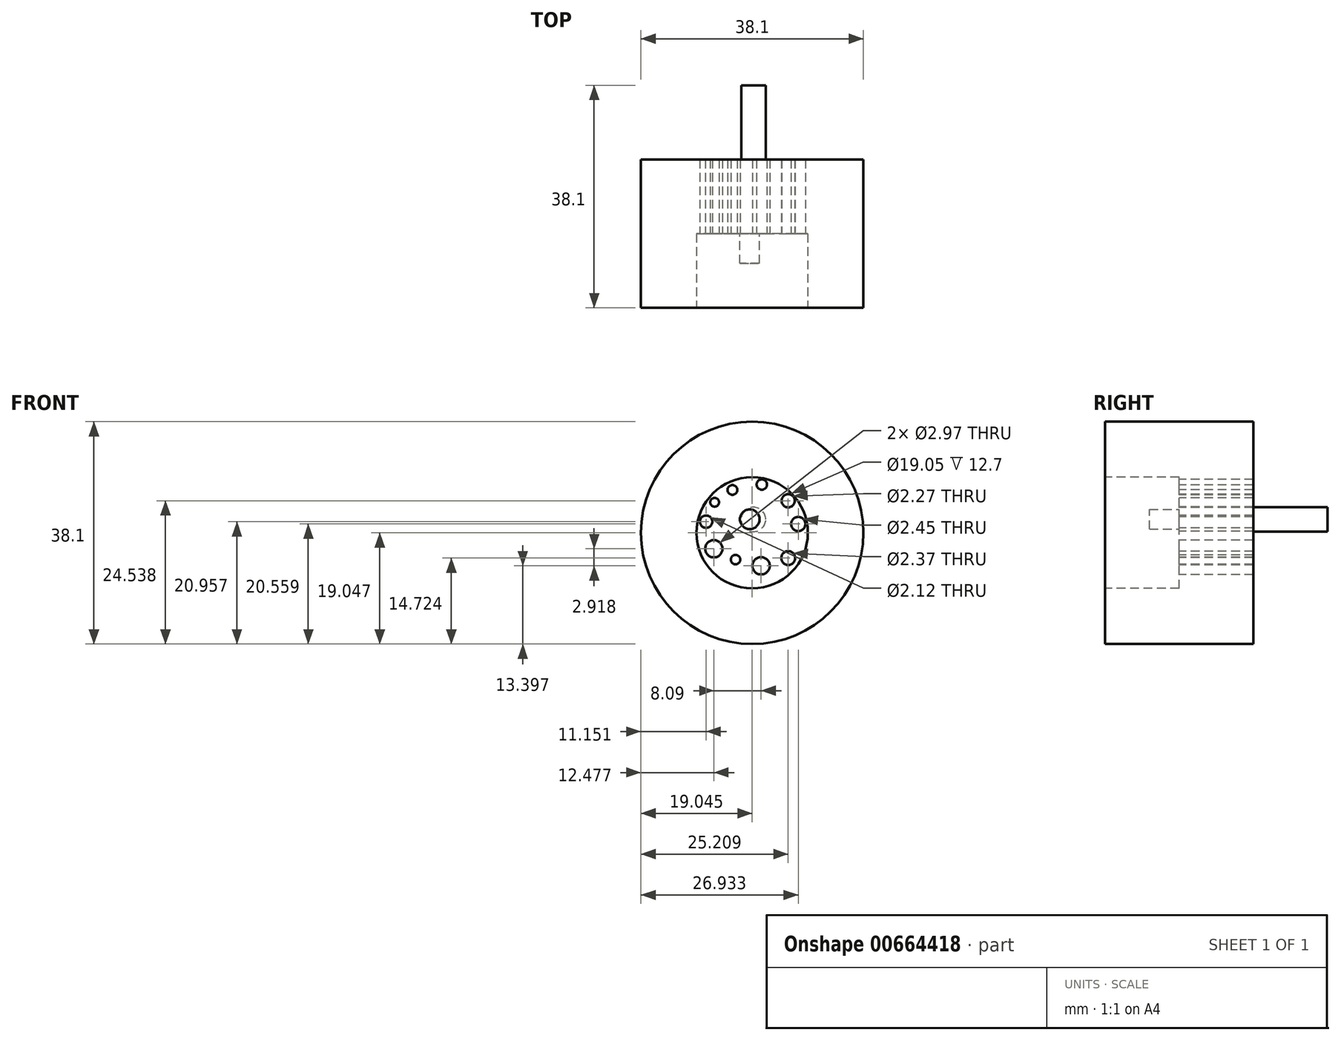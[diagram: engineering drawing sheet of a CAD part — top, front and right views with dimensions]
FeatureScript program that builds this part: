
annotation { "Feature Type Name" : "Feature", "Feature Type Description" : "" }
export const myFeature = defineFeature(function(context is Context, id is Id, definition is map)
    precondition{}
    {
        {
            var Q0;
            Q0=qCreatedBy(makeId("Front.planeOp"),FACE);
            var sketch = newSketch(context, id + "F0", { "sketchPlane" : qUnion([Q0])});
            skCircle(sketch, "E0", {"center": v(-47.62, 24.26) * mm, "radius": 19.05 * mm});
            skSolve(sketch);
        }
        {
            var Q0;
            Q0=makeQuery(id+"F0.imprint","IMPRINT",FACE,{"disambiguationData":[TD([[makeQuery(id+"F0.imprint","IMPRINT",EDGE,{"derivedFrom":sQuery(id+"F0.wireOp",EDGE,"E0")}),1.0]])]});
            extrude(context, id + "F1", {"entities" : qUnion([Q0]), "oppositeDirection" : true, "depth" : 25.4 * mm, "offsetDistance" : 25.4 * mm});
        }
        {
            var Q0;
            Q0=makeQuery(id+"F1.opExtrude","CAP_FACE",FACE,{"disambiguationData":[OSD([sQuery(id+"F0.wireOp",EDGE,"E0")])],"isStart":true});
            var sketch = newSketch(context, id + "F2", { "sketchPlane" : qUnion([Q0])});
            skCircle(sketch, "E1", {"center": v(-47.62, 24.26) * mm, "radius": 9.53 * mm});
            skSolve(sketch);
        }
        {
            var Q0;
            Q0=makeQuery(id+"F2.imprint","IMPRINT",FACE,{"disambiguationData":[TD([[makeQuery(id+"F2.imprint","IMPRINT",EDGE,{"derivedFrom":sQuery(id+"F2.wireOp",EDGE,"E1")}),1.0]])]});
            extrude(context, id + "F3", {"entities" : qUnion([Q0]), "operationType" : NewBodyOperationType.REMOVE, "oppositeDirection" : true, "depth" : 12.7 * mm, "offsetDistance" : 25.4 * mm});
        }
        {
            var Q0;
            Q0=makeQuery(id+"F3.boolean.opBoolean","COPY",FACE,{"derivedFrom":makeQuery(id+"F3.opExtrude","CAP_FACE",FACE,{"disambiguationData":[OSD([sQuery(id+"F2.wireOp",EDGE,"E1")])],"isStart":false})});
            var sketch = newSketch(context, id + "F4", { "sketchPlane" : qUnion([Q0])});
            skCircle(sketch, "E2", {"center": v(-54.06, 29.48) * mm, "radius": 0.75 * mm});
            skCircle(sketch, "E3", {"center": v(-51.01, 31.6) * mm, "radius": 0.84 * mm});
            skCircle(sketch, "E4", {"center": v(-45.97, 32.53) * mm, "radius": 0.89 * mm});
            skCircle(sketch, "E5", {"center": v(-41.46, 29.75) * mm, "radius": 1.13 * mm});
            skCircle(sketch, "E6", {"center": v(-39.74, 25.77) * mm, "radius": 1.22 * mm});
            skCircle(sketch, "E7", {"center": v(-41.46, 19.93) * mm, "radius": 1.19 * mm});
            skCircle(sketch, "E8", {"center": v(-46.1, 18.6) * mm, "radius": 1.48 * mm});
            skCircle(sketch, "E9", {"center": v(-54.2, 21.53) * mm, "radius": 1.48 * mm});
            skCircle(sketch, "E10", {"center": v(-55.52, 26.17) * mm, "radius": 1.06 * mm});
            skCircle(sketch, "E11", {"center": v(-50.48, 19.67) * mm, "radius": 0.8 * mm});
            skSolve(sketch);
        }
        {
            var Q0;
            Q0=makeQuery(id+"F4.imprint","IMPRINT",FACE,{"disambiguationData":[TD([[makeQuery(id+"F4.imprint","IMPRINT",EDGE,{"derivedFrom":sQuery(id+"F4.wireOp",EDGE,"E5")}),1.0]])]});
            var Q1;
            Q1=makeQuery(id+"F4.imprint","IMPRINT",FACE,{"disambiguationData":[TD([[makeQuery(id+"F4.imprint","IMPRINT",EDGE,{"derivedFrom":sQuery(id+"F4.wireOp",EDGE,"E4")}),1.0]])]});
            var Q2;
            Q2=makeQuery(id+"F4.imprint","IMPRINT",FACE,{"disambiguationData":[TD([[makeQuery(id+"F4.imprint","IMPRINT",EDGE,{"derivedFrom":sQuery(id+"F4.wireOp",EDGE,"E3")}),1.0]])]});
            var Q3;
            Q3=makeQuery(id+"F4.imprint","IMPRINT",FACE,{"disambiguationData":[TD([[makeQuery(id+"F4.imprint","IMPRINT",EDGE,{"derivedFrom":sQuery(id+"F4.wireOp",EDGE,"E2")}),1.0]])]});
            var Q4;
            Q4=makeQuery(id+"F4.imprint","IMPRINT",FACE,{"disambiguationData":[TD([[makeQuery(id+"F4.imprint","IMPRINT",EDGE,{"derivedFrom":sQuery(id+"F4.wireOp",EDGE,"E10")}),1.0]])]});
            var Q5;
            Q5=makeQuery(id+"F4.imprint","IMPRINT",FACE,{"disambiguationData":[TD([[makeQuery(id+"F4.imprint","IMPRINT",EDGE,{"derivedFrom":sQuery(id+"F4.wireOp",EDGE,"E9")}),1.0]])]});
            var Q6;
            Q6=makeQuery(id+"F4.imprint","IMPRINT",FACE,{"disambiguationData":[TD([[makeQuery(id+"F4.imprint","IMPRINT",EDGE,{"derivedFrom":sQuery(id+"F4.wireOp",EDGE,"E11")}),1.0]])]});
            var Q7;
            Q7=makeQuery(id+"F4.imprint","IMPRINT",FACE,{"disambiguationData":[TD([[makeQuery(id+"F4.imprint","IMPRINT",EDGE,{"derivedFrom":sQuery(id+"F4.wireOp",EDGE,"E8")}),1.0]])]});
            var Q8;
            Q8=makeQuery(id+"F4.imprint","IMPRINT",FACE,{"disambiguationData":[TD([[makeQuery(id+"F4.imprint","IMPRINT",EDGE,{"derivedFrom":sQuery(id+"F4.wireOp",EDGE,"E7")}),1.0]])]});
            var Q9;
            Q9=makeQuery(id+"F4.imprint","IMPRINT",FACE,{"disambiguationData":[TD([[makeQuery(id+"F4.imprint","IMPRINT",EDGE,{"derivedFrom":sQuery(id+"F4.wireOp",EDGE,"E6")}),1.0]])]});
            extrude(context, id + "F5", {"entities" : qUnion([Q0, Q1, Q2, Q3, Q4, Q5, Q6, Q7, Q8, Q9]), "operationType" : NewBodyOperationType.REMOVE, "oppositeDirection" : true, "depth" : 25.4 * mm, "offsetDistance" : 25.4 * mm});
        }
        {
            var Q0;
            Q0=makeQuery(id+"F3.boolean.opBoolean","COPY",FACE,{"derivedFrom":makeQuery(id+"F3.opExtrude","CAP_FACE",FACE,{"disambiguationData":[OSD([sQuery(id+"F2.wireOp",EDGE,"E1")])],"isStart":false})});
            var sketch = newSketch(context, id + "F6", { "sketchPlane" : qUnion([Q0])});
            skCircle(sketch, "E12", {"center": v(-47.95, 26.44) * mm, "radius": 2.57 * mm});
            skSolve(sketch);
        }
        {
            var Q0;
            Q0=makeQuery(id+"F6.imprint","IMPRINT",FACE,{"disambiguationData":[TD([[makeQuery(id+"F6.imprint","IMPRINT",EDGE,{"derivedFrom":sQuery(id+"F6.wireOp",EDGE,"E12")}),1.0]])]});
            var sketch = newSketch(context, id + "F7", { "sketchPlane" : qUnion([Q0])});
            skCircle(sketch, "E13", {"center": v(-48.04, 26.58) * mm, "radius": 1.68 * mm});
            skSolve(sketch);
        }
        {
            var Q0;
            Q0 = qSketchRegion(id + "F7", true);
            extrude(context, id + "F8", {"entities" : qUnion([Q0]), "operationType" : NewBodyOperationType.ADD, "depth" : 5.08 * mm, "offsetDistance" : 25.4 * mm});
        }
        {
            var Q0;
            Q0=makeQuery(id+"F1.opExtrude","CAP_FACE",FACE,{"disambiguationData":[OSD([sQuery(id+"F0.wireOp",EDGE,"E0")])],"isStart":false});
            var sketch = newSketch(context, id + "F9", { "sketchPlane" : qUnion([Q0])});
            skCircle(sketch, "E14", {"center": v(47.41, 26.55) * mm, "radius": 2.1 * mm});
            skSolve(sketch);
        }
        {
            var Q0;
            Q0=makeQuery(id+"F9.imprint","IMPRINT",FACE,{"disambiguationData":[TD([[makeQuery(id+"F9.imprint","IMPRINT",EDGE,{"derivedFrom":sQuery(id+"F9.wireOp",EDGE,"E14")}),1.0]])]});
            extrude(context, id + "F10", {"entities" : qUnion([Q0]), "operationType" : NewBodyOperationType.ADD, "depth" : 12.7 * mm, "offsetDistance" : 25.4 * mm});
        }
    });
